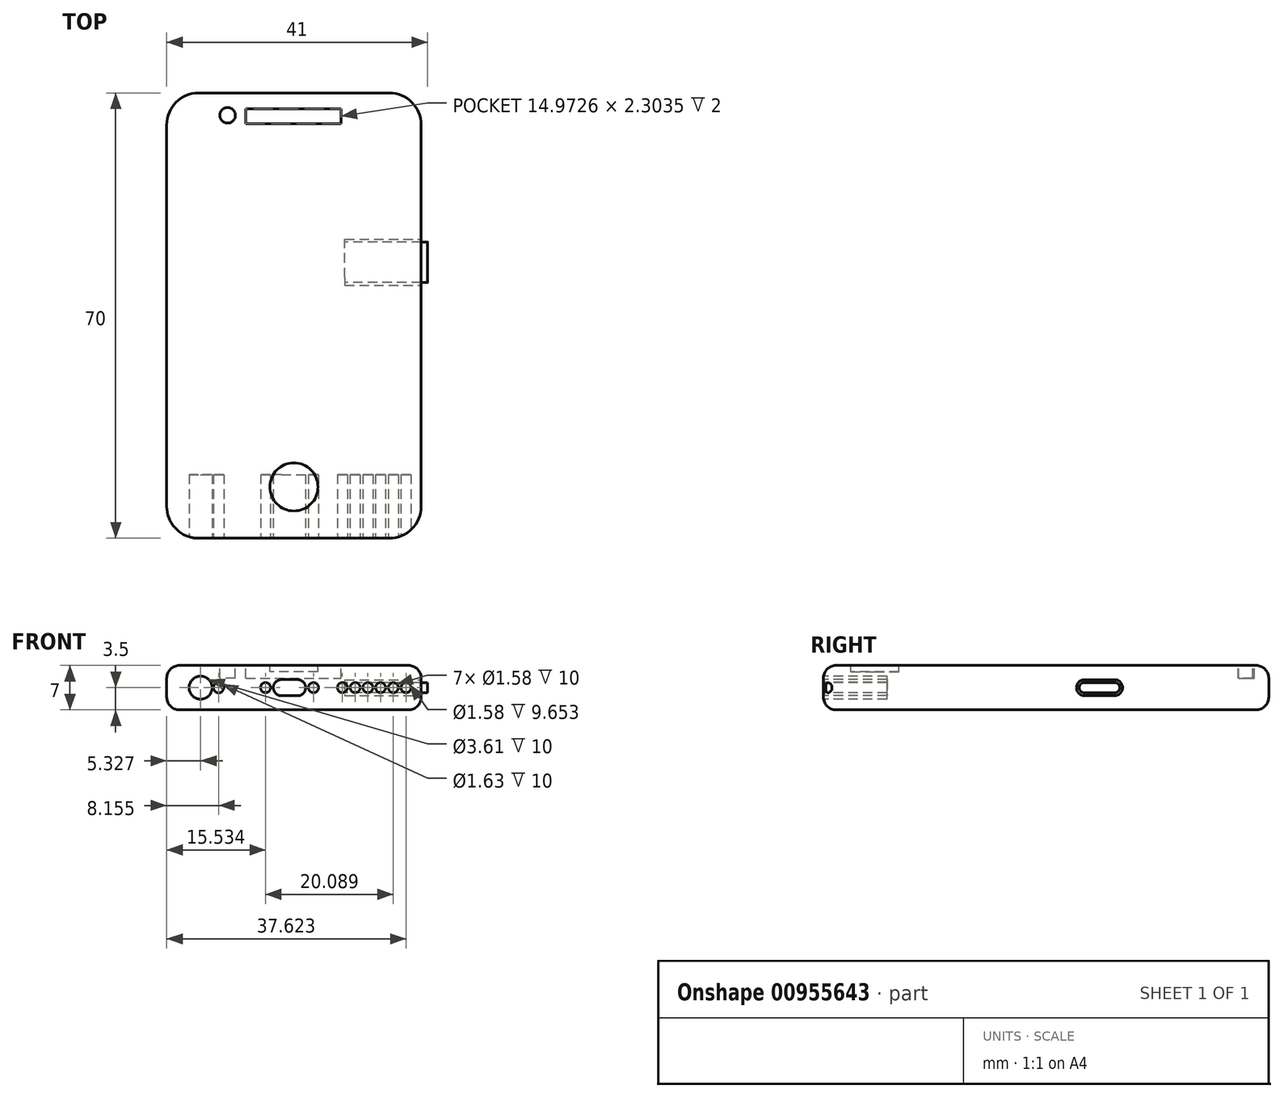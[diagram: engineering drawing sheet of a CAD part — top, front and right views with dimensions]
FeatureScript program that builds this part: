
annotation { "Feature Type Name" : "Feature", "Feature Type Description" : "" }
export const myFeature = defineFeature(function(context is Context, id is Id, definition is map)
    precondition{}
    {
        {
            var Q0;
            Q0=qCreatedBy(makeId("Top.planeOp"),FACE);
            var sketch = newSketch(context, id + "F0", { "sketchPlane" : qUnion([Q0])});
            skLineSegment(sketch, "E0.bottom", {"start": v(0, 0) * mm, "end": v(40, 0) * mm});
            skLineSegment(sketch, "E0.top", {"start": v(0, 70) * mm, "end": v(40, 70) * mm});
            skLineSegment(sketch, "E0.left", {"start": v(0, 0) * mm, "end": v(0, 70) * mm});
            skLineSegment(sketch, "E0.right", {"start": v(40, 0) * mm, "end": v(40, 70) * mm});
            skSolve(sketch);
        }
        {
            var Q0;
            Q0=makeQuery(id+"F0.imprint","IMPRINT",FACE,{"disambiguationData":[TD([[makeQuery(id+"F0.imprint","IMPRINT",EDGE,{"derivedFrom":sQuery(id+"F0.wireOp",EDGE,"E0.bottom")}),1.0]])]});
            extrude(context, id + "F1", {"entities" : qUnion([Q0]), "depth" : 7 * mm, "offsetDistance" : 25 * mm});
        }
        {
            var Q0;
            Q0=makeQuery(id+"F1.opExtrude","SWEPT_FACE",FACE,{"disambiguationData":[OSD([sQuery(id+"F0.wireOp",EDGE,"E0.bottom")])]});
            var sketch = newSketch(context, id + "F2", { "sketchPlane" : qUnion([Q0])});
            skCircle(sketch, "E1", {"center": v(5.33, 3.5) * mm, "radius": 1.8 * mm});
            skPoint(sketch, "E1.centerSnap0", {"position": v(0, 3.5) * mm});
            skCircle(sketch, "E2", {"center": v(8.15, 3.5) * mm, "radius": 0.82 * mm});
            skCircle(sketch, "E3", {"center": v(15.53, 3.5) * mm, "radius": 0.79 * mm});
            skArc(sketch, "E4", {"start": v(18.05, 4.78) * mm, "mid": v(16.77, 3.5) * mm, "end": v(18.05, 2.22) * mm});
            skCircle(sketch, "E5", {"center": v(23.07, 3.5) * mm, "radius": 0.79 * mm});
            skCircle(sketch, "E6", {"center": v(27.62, 3.5) * mm, "radius": 0.79 * mm});
            skLineSegment(sketch, "E7", {"start": v(18.05, 4.78) * mm, "end": v(20.56, 4.78) * mm});
            skLineSegment(sketch, "E8", {"start": v(18.05, 2.22) * mm, "end": v(20.56, 2.22) * mm});
            skArc(sketch, "E9.trimOffspring", {"start": v(20.56, 2.22) * mm, "mid": v(21.84, 3.5) * mm, "end": v(20.56, 4.78) * mm});
            skCircle(sketch, "E10.1.0.0", {"center": v(29.62, 3.5) * mm, "radius": 0.79 * mm});
            skCircle(sketch, "E10.2.0.0", {"center": v(31.62, 3.5) * mm, "radius": 0.79 * mm});
            skCircle(sketch, "E10.3.0.0", {"center": v(33.62, 3.5) * mm, "radius": 0.79 * mm});
            skCircle(sketch, "E10.4.0.0", {"center": v(35.62, 3.5) * mm, "radius": 0.79 * mm});
            skCircle(sketch, "E10.5.0.0", {"center": v(37.62, 3.5) * mm, "radius": 0.79 * mm});
            skLineSegment(sketch, "E10.direction1", {"start": v(27.62, 3.5) * mm, "end": v(29.62, 3.5) * mm, "construction": true});
            skSolve(sketch);
        }
        {
            var Q0;
            Q0=makeQuery(id+"F2.imprint","IMPRINT",FACE,{"disambiguationData":[TD([[makeQuery(id+"F2.imprint","IMPRINT",EDGE,{"derivedFrom":sQuery(id+"F2.wireOp",EDGE,"E3")}),1.0]])]});
            var Q1;
            Q1=makeQuery(id+"F2.imprint","IMPRINT",FACE,{"disambiguationData":[TD([[makeQuery(id+"F2.imprint","IMPRINT",EDGE,{"derivedFrom":sQuery(id+"F2.wireOp",EDGE,"E4")}),1.0]])]});
            var Q2;
            Q2=makeQuery(id+"F2.imprint","IMPRINT",FACE,{"disambiguationData":[TD([[makeQuery(id+"F2.imprint","IMPRINT",EDGE,{"derivedFrom":sQuery(id+"F2.wireOp",EDGE,"E6")}),1.0]])]});
            var Q3;
            Q3=makeQuery(id+"F2.imprint","IMPRINT",FACE,{"disambiguationData":[TD([[makeQuery(id+"F2.imprint","IMPRINT",EDGE,{"derivedFrom":sQuery(id+"F2.wireOp",EDGE,"E5")}),1.0]])]});
            var Q4;
            Q4=makeQuery(id+"F2.imprint","IMPRINT",FACE,{"disambiguationData":[TD([[makeQuery(id+"F2.imprint","IMPRINT",EDGE,{"derivedFrom":sQuery(id+"F2.wireOp",EDGE,"E10.1.0.0")}),1.0]])]});
            var Q5;
            Q5=makeQuery(id+"F2.imprint","IMPRINT",FACE,{"disambiguationData":[TD([[makeQuery(id+"F2.imprint","IMPRINT",EDGE,{"derivedFrom":sQuery(id+"F2.wireOp",EDGE,"E10.2.0.0")}),1.0]])]});
            var Q6;
            Q6=makeQuery(id+"F2.imprint","IMPRINT",FACE,{"disambiguationData":[TD([[makeQuery(id+"F2.imprint","IMPRINT",EDGE,{"derivedFrom":sQuery(id+"F2.wireOp",EDGE,"E10.3.0.0")}),1.0]])]});
            var Q7;
            Q7=makeQuery(id+"F2.imprint","IMPRINT",FACE,{"disambiguationData":[TD([[makeQuery(id+"F2.imprint","IMPRINT",EDGE,{"derivedFrom":sQuery(id+"F2.wireOp",EDGE,"E10.4.0.0")}),1.0]])]});
            var Q8;
            Q8=makeQuery(id+"F2.imprint","IMPRINT",FACE,{"disambiguationData":[TD([[makeQuery(id+"F2.imprint","IMPRINT",EDGE,{"derivedFrom":sQuery(id+"F2.wireOp",EDGE,"E10.5.0.0")}),1.0]])]});
            var Q9;
            Q9=makeQuery(id+"F2.imprint","IMPRINT",FACE,{"disambiguationData":[TD([[makeQuery(id+"F2.imprint","IMPRINT",EDGE,{"derivedFrom":sQuery(id+"F2.wireOp",EDGE,"E1")}),1.0]])]});
            var Q10;
            Q10=makeQuery(id+"F2.imprint","IMPRINT",FACE,{"disambiguationData":[TD([[makeQuery(id+"F2.imprint","IMPRINT",EDGE,{"derivedFrom":sQuery(id+"F2.wireOp",EDGE,"E2")}),1.0]])]});
            extrude(context, id + "F3", {"entities" : qUnion([Q0, Q1, Q2, Q3, Q4, Q5, Q6, Q7, Q8, Q9, Q10]), "operationType" : NewBodyOperationType.REMOVE, "oppositeDirection" : true, "depth" : 10 * mm, "offsetDistance" : 25 * mm});
        }
        {
            var Q0;
            Q0=makeQuery(id+"F1.opExtrude","SWEPT_FACE",FACE,{"disambiguationData":[OSD([sQuery(id+"F0.wireOp",EDGE,"E0.right")])]});
            var sketch = newSketch(context, id + "F4", { "sketchPlane" : qUnion([Q0])});
            skArc(sketch, "E11", {"start": v(41.02, 4.75) * mm, "mid": v(39.77, 3.5) * mm, "end": v(41.02, 2.25) * mm});
            skPoint(sketch, "E11.centerSnap0", {"position": v(0, 3.5) * mm});
            skArc(sketch, "E12", {"start": v(45.77, 2.25) * mm, "mid": v(47.02, 3.5) * mm, "end": v(45.77, 4.75) * mm});
            skLineSegment(sketch, "E13", {"start": v(41.02, 4.75) * mm, "end": v(45.77, 4.75) * mm});
            skLineSegment(sketch, "E14", {"start": v(41.02, 2.25) * mm, "end": v(45.77, 2.25) * mm});
            skSolve(sketch);
        }
        {
            var Q0;
            Q0=makeQuery(id+"F4.imprint","IMPRINT",FACE,{"disambiguationData":[TD([[makeQuery(id+"F4.imprint","IMPRINT",EDGE,{"derivedFrom":sQuery(id+"F4.wireOp",EDGE,"E11")}),1.0]])]});
            extrude(context, id + "F5", {"entities" : qUnion([Q0]), "operationType" : NewBodyOperationType.REMOVE, "oppositeDirection" : true, "depth" : 12 * mm, "offsetDistance" : 25 * mm});
        }
        {
            var Q0;
            Q0=makeQuery(id+"F5.boolean.opBoolean","COPY",FACE,{"derivedFrom":makeQuery(id+"F5.opExtrude","CAP_FACE",FACE,{"disambiguationData":[OSD([sQuery(id+"F4.wireOp",EDGE,"E11"),sQuery(id+"F4.wireOp",EDGE,"E12"),sQuery(id+"F4.wireOp",EDGE,"E13"),sQuery(id+"F4.wireOp",EDGE,"E14")])],"isStart":false})});
            var sketch = newSketch(context, id + "F6", { "sketchPlane" : qUnion([Q0])});
            skArc(sketch, "E15", {"start": v(41.02, 4.31) * mm, "mid": v(40.2, 3.5) * mm, "end": v(41.02, 2.69) * mm});
            skArc(sketch, "E16", {"start": v(45.77, 2.7) * mm, "mid": v(46.57, 3.5) * mm, "end": v(45.77, 4.3) * mm});
            skLineSegment(sketch, "E17", {"start": v(41.02, 2.69) * mm, "end": v(45.77, 2.7) * mm});
            skLineSegment(sketch, "E18", {"start": v(41.02, 4.31) * mm, "end": v(45.77, 4.3) * mm});
            skSolve(sketch);
        }
        {
            var Q0;
            {var subQ3=sQuery(id+"F6.wireOp",EDGE,"E15");Q0=makeQuery(id+"F6.imprint","IMPRINT",FACE,{"disambiguationData":[TD([[makeQuery(id+"F6.imprint","IMPRINT",EDGE,{"derivedFrom":subQ3}),1.0]])]});}
            extrude(context, id + "F7", {"entities" : qUnion([Q0]), "operationType" : NewBodyOperationType.ADD, "depth" : 13 * mm, "offsetDistance" : 25 * mm});
        }
        {
            var Q0;
            Q0=makeQuery(id+"F1.opExtrude","CAP_FACE",FACE,{"disambiguationData":[OSD([sQuery(id+"F0.wireOp",EDGE,"E0.bottom"),sQuery(id+"F0.wireOp",EDGE,"E0.top"),sQuery(id+"F0.wireOp",EDGE,"E0.left"),sQuery(id+"F0.wireOp",EDGE,"E0.right")])],"isStart":false});
            var sketch = newSketch(context, id + "F8", { "sketchPlane" : qUnion([Q0])});
            skCircle(sketch, "E19", {"center": v(20, 8.06) * mm, "radius": 3.78 * mm});
            skPoint(sketch, "E19.centerSnap0", {"position": v(20, 0) * mm});
            skSolve(sketch);
        }
        {
            var Q0;
            Q0=makeQuery(id+"F8.imprint","IMPRINT",FACE,{"disambiguationData":[TD([[makeQuery(id+"F8.imprint","IMPRINT",EDGE,{"derivedFrom":sQuery(id+"F8.wireOp",EDGE,"E19")}),1.0]])]});
            extrude(context, id + "F9", {"entities" : qUnion([Q0]), "operationType" : NewBodyOperationType.REMOVE, "oppositeDirection" : true, "depth" : 1 * mm, "offsetDistance" : 25 * mm});
        }
        {
            var Q0;
            Q0=makeQuery(id+"F1.opExtrude","CAP_FACE",FACE,{"disambiguationData":[OSD([sQuery(id+"F0.wireOp",EDGE,"E0.bottom"),sQuery(id+"F0.wireOp",EDGE,"E0.top"),sQuery(id+"F0.wireOp",EDGE,"E0.left"),sQuery(id+"F0.wireOp",EDGE,"E0.right")])],"isStart":false});
            var sketch = newSketch(context, id + "F10", { "sketchPlane" : qUnion([Q0])});
            skLineSegment(sketch, "E20.bottom", {"start": v(12.42, 67.5) * mm, "end": v(27.4, 67.5) * mm});
            skLineSegment(sketch, "E20.top", {"start": v(12.42, 65.2) * mm, "end": v(27.4, 65.2) * mm});
            skLineSegment(sketch, "E20.left", {"start": v(12.42, 67.5) * mm, "end": v(12.42, 65.2) * mm});
            skLineSegment(sketch, "E20.right", {"start": v(27.4, 67.5) * mm, "end": v(27.4, 65.2) * mm});
            skCircle(sketch, "E21", {"center": v(9.57, 66.49) * mm, "radius": 1.22 * mm});
            skSolve(sketch);
        }
        {
            var Q0;
            Q0=makeQuery(id+"F10.imprint","IMPRINT",FACE,{"disambiguationData":[TD([[makeQuery(id+"F10.imprint","IMPRINT",EDGE,{"derivedFrom":sQuery(id+"F10.wireOp",EDGE,"E20.bottom")}),-1.0]])]});
            var Q1;
            Q1=makeQuery(id+"F10.imprint","IMPRINT",FACE,{"disambiguationData":[TD([[makeQuery(id+"F10.imprint","IMPRINT",EDGE,{"derivedFrom":sQuery(id+"F10.wireOp",EDGE,"E21")}),1.0]])]});
            extrude(context, id + "F11", {"entities" : qUnion([Q0, Q1]), "operationType" : NewBodyOperationType.REMOVE, "oppositeDirection" : true, "depth" : 2 * mm, "offsetDistance" : 25 * mm});
        }
        {
            var Q0;
            Q0=makeQuery(id+"F1.opExtrude","SWEPT_EDGE",EDGE,{"disambiguationData":[OSD([sQuery(id+"F0.wireOp",EDGE,"E0.bottom"),sQuery(id+"F0.wireOp",EDGE,"E0.left")])]});
            fillet(context, id + "F12", {"entities" : qUnion([Q0]), "radius" : 5 * mm, "tangentPropagation" : true, "allowEdgeOverflow" : false});
        }
        {
            var Q0;
            Q0=makeQuery(id+"F1.opExtrude","SWEPT_EDGE",EDGE,{"disambiguationData":[OSD([sQuery(id+"F0.wireOp",EDGE,"E0.top"),sQuery(id+"F0.wireOp",EDGE,"E0.left")])]});
            fillet(context, id + "F13", {"entities" : qUnion([Q0]), "radius" : 5 * mm, "tangentPropagation" : true, "allowEdgeOverflow" : false});
        }
        {
            var Q0;
            Q0=makeQuery(id+"F1.opExtrude","SWEPT_EDGE",EDGE,{"disambiguationData":[OSD([sQuery(id+"F0.wireOp",EDGE,"E0.top"),sQuery(id+"F0.wireOp",EDGE,"E0.right")])]});
            fillet(context, id + "F14", {"entities" : qUnion([Q0]), "radius" : 5 * mm, "tangentPropagation" : true, "allowEdgeOverflow" : false});
        }
        {
            var Q0;
            Q0=makeQuery(id+"F1.opExtrude","SWEPT_EDGE",EDGE,{"disambiguationData":[OSD([sQuery(id+"F0.wireOp",EDGE,"E0.bottom"),sQuery(id+"F0.wireOp",EDGE,"E0.right")])]});
            fillet(context, id + "F15", {"entities" : qUnion([Q0]), "radius" : 5 * mm, "tangentPropagation" : true, "allowEdgeOverflow" : false});
        }
        {
            var Q0;
            Q0=makeQuery(id+"F1.opExtrude","CAP_EDGE",EDGE,{"disambiguationData":[OSD([sQuery(id+"F0.wireOp",EDGE,"E0.right")])],"isStart":false});
            var Q1;
            Q1=makeQuery(id+"F1.opExtrude","CAP_EDGE",EDGE,{"disambiguationData":[OSD([sQuery(id+"F0.wireOp",EDGE,"E0.left")])],"isStart":false});
            fillet(context, id + "F16", {"entities" : qUnion([Q0, Q1]), "radius" : 2 * mm, "tangentPropagation" : true, "allowEdgeOverflow" : false});
        }
        {
            var Q0;
            Q0=makeQuery(id+"F1.opExtrude","CAP_EDGE",EDGE,{"disambiguationData":[OSD([sQuery(id+"F0.wireOp",EDGE,"E0.left")])],"isStart":true});
            var Q1;
            Q1=makeQuery(id+"F1.opExtrude","CAP_EDGE",EDGE,{"disambiguationData":[OSD([sQuery(id+"F0.wireOp",EDGE,"E0.right")])],"isStart":true});
            fillet(context, id + "F17", {"entities" : qUnion([Q0, Q1]), "radius" : 2 * mm, "tangentPropagation" : true, "allowEdgeOverflow" : false});
        }
    });
